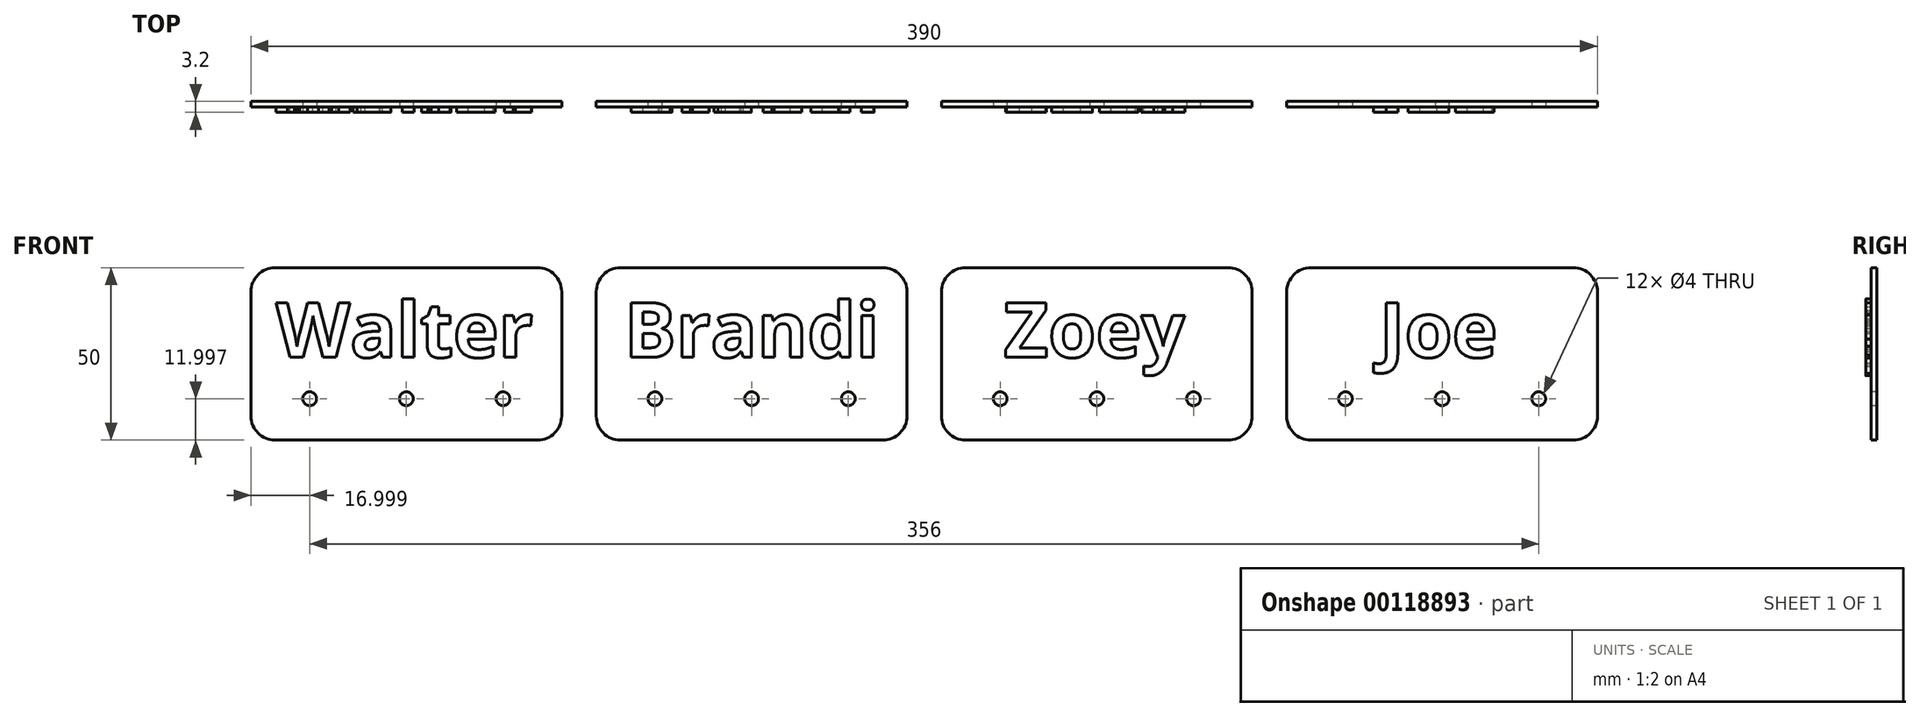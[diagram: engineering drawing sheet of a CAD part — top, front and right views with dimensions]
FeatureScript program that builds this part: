
annotation { "Feature Type Name" : "Feature", "Feature Type Description" : "" }
export const myFeature = defineFeature(function(context is Context, id is Id, definition is map)
    precondition{}
    {
        {
            var Q0;
            Q0=qCreatedBy(makeId("Front.planeOp"),FACE);
            var sketch = newSketch(context, id + "F0", { "sketchPlane" : qUnion([Q0])});
            skLineSegment(sketch, "E0.bottom", {"start": v(-28.01, 48.34) * mm, "end": v(47.99, 48.34) * mm});
            skLineSegment(sketch, "E0.top", {"start": v(-28.01, -1.66) * mm, "end": v(47.99, -1.66) * mm});
            skLineSegment(sketch, "E0.left", {"start": v(-35.01, 41.34) * mm, "end": v(-35.01, 5.34) * mm});
            skLineSegment(sketch, "E0.right", {"start": v(54.99, 41.34) * mm, "end": v(54.99, 5.34) * mm});
            skLineSegment(sketch, "E1", {"start": v(-35.01, 10.34) * mm, "end": v(54.99, 10.34) * mm, "construction": true});
            skLineSegment(sketch, "E2", {"start": v(-35.01, 22.34) * mm, "end": v(54.99, 22.34) * mm, "construction": true});
            skLineSegment(sketch, "E3", {"start": v(-35.01, 38.34) * mm, "end": v(54.99, 38.34) * mm, "construction": true});
            skPoint(sketch, "E4.visualSharp", {"position": v(-35.01, 48.34) * mm});
            skArc(sketch, "E4.filletArc", {"start": v(-28.01, 48.34) * mm, "mid": v(-32.96, 46.29) * mm, "end": v(-35.01, 41.34) * mm});
            skPoint(sketch, "E5.visualSharp", {"position": v(54.99, 48.34) * mm});
            skArc(sketch, "E5.filletArc", {"start": v(54.99, 41.34) * mm, "mid": v(52.94, 46.29) * mm, "end": v(47.99, 48.34) * mm});
            skPoint(sketch, "E6.visualSharp", {"position": v(54.99, -1.66) * mm});
            skArc(sketch, "E6.filletArc", {"start": v(47.99, -1.66) * mm, "mid": v(52.94, 0.39) * mm, "end": v(54.99, 5.34) * mm});
            skPoint(sketch, "E7.visualSharp", {"position": v(-35.01, -1.66) * mm});
            skArc(sketch, "E7.filletArc", {"start": v(-35.01, 5.34) * mm, "mid": v(-32.96, 0.39) * mm, "end": v(-28.01, -1.66) * mm});
            skLineSegment(sketch, "E8", {"start": v(9.99, 48.34) * mm, "end": v(9.99, -1.66) * mm, "construction": true});
            skCircle(sketch, "E9", {"center": v(-18.01, 10.34) * mm, "radius": 2 * mm});
            skCircle(sketch, "E10", {"center": v(9.99, 10.34) * mm, "radius": 2 * mm});
            skCircle(sketch, "E11.MirrorC", {"center": v(37.99, 10.34) * mm, "radius": 2 * mm});
            skLineSegment(sketch, "E12.1.0.0", {"start": v(64.99, 41.34) * mm, "end": v(64.99, 5.34) * mm});
            skArc(sketch, "E12.1.0.1", {"start": v(71.99, 48.34) * mm, "mid": v(67.04, 46.29) * mm, "end": v(64.99, 41.34) * mm});
            skPoint(sketch, "E12.1.0.2", {"position": v(154.99, -1.66) * mm});
            skLineSegment(sketch, "E12.1.0.3", {"start": v(64.99, 38.34) * mm, "end": v(154.99, 38.34) * mm, "construction": true});
            skArc(sketch, "E12.1.0.4", {"start": v(147.99, -1.66) * mm, "mid": v(152.94, 0.39) * mm, "end": v(154.99, 5.34) * mm});
            skLineSegment(sketch, "E12.1.0.5", {"start": v(64.99, 22.34) * mm, "end": v(154.99, 22.34) * mm, "construction": true});
            skLineSegment(sketch, "E12.1.0.6", {"start": v(64.99, 10.34) * mm, "end": v(154.99, 10.34) * mm, "construction": true});
            skLineSegment(sketch, "E12.1.0.7", {"start": v(154.99, 41.34) * mm, "end": v(154.99, 5.34) * mm});
            skArc(sketch, "E12.1.0.8", {"start": v(64.99, 5.34) * mm, "mid": v(67.04, 0.39) * mm, "end": v(71.99, -1.66) * mm});
            skLineSegment(sketch, "E12.1.0.9", {"start": v(109.99, 48.34) * mm, "end": v(109.99, -1.66) * mm, "construction": true});
            skLineSegment(sketch, "E12.1.0.10", {"start": v(71.99, -1.66) * mm, "end": v(147.99, -1.66) * mm});
            skPoint(sketch, "E12.1.0.11", {"position": v(154.99, 48.34) * mm});
            skCircle(sketch, "E12.1.0.12", {"center": v(81.99, 10.34) * mm, "radius": 2 * mm});
            skCircle(sketch, "E12.1.0.13", {"center": v(109.99, 10.34) * mm, "radius": 2 * mm});
            skArc(sketch, "E12.1.0.14", {"start": v(154.99, 41.34) * mm, "mid": v(152.94, 46.29) * mm, "end": v(147.99, 48.34) * mm});
            skCircle(sketch, "E12.1.0.15", {"center": v(137.99, 10.34) * mm, "radius": 2 * mm});
            skPoint(sketch, "E12.1.0.16", {"position": v(64.99, 48.34) * mm});
            skLineSegment(sketch, "E12.1.0.17", {"start": v(71.99, 48.34) * mm, "end": v(147.99, 48.34) * mm});
            skPoint(sketch, "E12.1.0.18", {"position": v(64.99, -1.66) * mm});
            skLineSegment(sketch, "E12.2.0.0", {"start": v(164.99, 41.34) * mm, "end": v(164.99, 5.34) * mm});
            skArc(sketch, "E12.2.0.1", {"start": v(171.99, 48.34) * mm, "mid": v(167.04, 46.29) * mm, "end": v(164.99, 41.34) * mm});
            skPoint(sketch, "E12.2.0.2", {"position": v(254.99, -1.66) * mm});
            skLineSegment(sketch, "E12.2.0.3", {"start": v(164.99, 38.34) * mm, "end": v(254.99, 38.34) * mm, "construction": true});
            skArc(sketch, "E12.2.0.4", {"start": v(247.99, -1.66) * mm, "mid": v(252.94, 0.39) * mm, "end": v(254.99, 5.34) * mm});
            skLineSegment(sketch, "E12.2.0.5", {"start": v(164.99, 22.34) * mm, "end": v(254.99, 22.34) * mm, "construction": true});
            skLineSegment(sketch, "E12.2.0.6", {"start": v(164.99, 10.34) * mm, "end": v(254.99, 10.34) * mm, "construction": true});
            skLineSegment(sketch, "E12.2.0.7", {"start": v(254.99, 41.34) * mm, "end": v(254.99, 5.34) * mm});
            skArc(sketch, "E12.2.0.8", {"start": v(164.99, 5.34) * mm, "mid": v(167.04, 0.39) * mm, "end": v(171.99, -1.66) * mm});
            skLineSegment(sketch, "E12.2.0.9", {"start": v(209.99, 48.34) * mm, "end": v(209.99, -1.66) * mm, "construction": true});
            skLineSegment(sketch, "E12.2.0.10", {"start": v(171.99, -1.66) * mm, "end": v(247.99, -1.66) * mm});
            skPoint(sketch, "E12.2.0.11", {"position": v(254.99, 48.34) * mm});
            skCircle(sketch, "E12.2.0.12", {"center": v(181.99, 10.34) * mm, "radius": 2 * mm});
            skCircle(sketch, "E12.2.0.13", {"center": v(209.99, 10.34) * mm, "radius": 2 * mm});
            skArc(sketch, "E12.2.0.14", {"start": v(254.99, 41.34) * mm, "mid": v(252.94, 46.29) * mm, "end": v(247.99, 48.34) * mm});
            skCircle(sketch, "E12.2.0.15", {"center": v(237.99, 10.34) * mm, "radius": 2 * mm});
            skPoint(sketch, "E12.2.0.16", {"position": v(164.99, 48.34) * mm});
            skLineSegment(sketch, "E12.2.0.17", {"start": v(171.99, 48.34) * mm, "end": v(247.99, 48.34) * mm});
            skPoint(sketch, "E12.2.0.18", {"position": v(164.99, -1.66) * mm});
            skLineSegment(sketch, "E12.3.0.0", {"start": v(264.99, 41.34) * mm, "end": v(264.99, 5.34) * mm});
            skArc(sketch, "E12.3.0.1", {"start": v(271.99, 48.34) * mm, "mid": v(267.04, 46.29) * mm, "end": v(264.99, 41.34) * mm});
            skPoint(sketch, "E12.3.0.2", {"position": v(354.99, -1.66) * mm});
            skLineSegment(sketch, "E12.3.0.3", {"start": v(264.99, 38.34) * mm, "end": v(354.99, 38.34) * mm, "construction": true});
            skArc(sketch, "E12.3.0.4", {"start": v(347.99, -1.66) * mm, "mid": v(352.94, 0.39) * mm, "end": v(354.99, 5.34) * mm});
            skLineSegment(sketch, "E12.3.0.5", {"start": v(264.99, 22.34) * mm, "end": v(354.99, 22.34) * mm, "construction": true});
            skLineSegment(sketch, "E12.3.0.6", {"start": v(264.99, 10.34) * mm, "end": v(354.99, 10.34) * mm, "construction": true});
            skLineSegment(sketch, "E12.3.0.7", {"start": v(354.99, 41.34) * mm, "end": v(354.99, 5.34) * mm});
            skArc(sketch, "E12.3.0.8", {"start": v(264.99, 5.34) * mm, "mid": v(267.04, 0.39) * mm, "end": v(271.99, -1.66) * mm});
            skLineSegment(sketch, "E12.3.0.9", {"start": v(309.99, 48.34) * mm, "end": v(309.99, -1.66) * mm, "construction": true});
            skLineSegment(sketch, "E12.3.0.10", {"start": v(271.99, -1.66) * mm, "end": v(347.99, -1.66) * mm});
            skPoint(sketch, "E12.3.0.11", {"position": v(354.99, 48.34) * mm});
            skCircle(sketch, "E12.3.0.12", {"center": v(281.99, 10.34) * mm, "radius": 2 * mm});
            skCircle(sketch, "E12.3.0.13", {"center": v(309.99, 10.34) * mm, "radius": 2 * mm});
            skArc(sketch, "E12.3.0.14", {"start": v(354.99, 41.34) * mm, "mid": v(352.94, 46.29) * mm, "end": v(347.99, 48.34) * mm});
            skCircle(sketch, "E12.3.0.15", {"center": v(337.99, 10.34) * mm, "radius": 2 * mm});
            skPoint(sketch, "E12.3.0.16", {"position": v(264.99, 48.34) * mm});
            skLineSegment(sketch, "E12.3.0.17", {"start": v(271.99, 48.34) * mm, "end": v(347.99, 48.34) * mm});
            skPoint(sketch, "E12.3.0.18", {"position": v(264.99, -1.66) * mm});
            skLineSegment(sketch, "E12.direction1", {"start": v(-35.01, -1.66) * mm, "end": v(64.99, -1.66) * mm, "construction": true});
            skSolve(sketch);
        }
        {
            var Q0;
            Q0=makeQuery(id+"F0.imprint","IMPRINT",FACE,{"disambiguationData":[TD([[makeQuery(id+"F0.imprint","IMPRINT",EDGE,{"derivedFrom":sQuery(id+"F0.wireOp",EDGE,"E12.1.0.0")}),1.0]])]});
            var Q1;
            Q1=makeQuery(id+"F0.imprint","IMPRINT",FACE,{"disambiguationData":[TD([[makeQuery(id+"F0.imprint","IMPRINT",EDGE,{"derivedFrom":sQuery(id+"F0.wireOp",EDGE,"E12.2.0.0")}),1.0]])]});
            var Q2;
            Q2=makeQuery(id+"F0.imprint","IMPRINT",FACE,{"disambiguationData":[TD([[makeQuery(id+"F0.imprint","IMPRINT",EDGE,{"derivedFrom":sQuery(id+"F0.wireOp",EDGE,"E0.bottom")}),-1.0]])]});
            var Q3;
            Q3=makeQuery(id+"F0.imprint","IMPRINT",FACE,{"disambiguationData":[TD([[makeQuery(id+"F0.imprint","IMPRINT",EDGE,{"derivedFrom":sQuery(id+"F0.wireOp",EDGE,"E12.3.0.0")}),1.0]])]});
            extrude(context, id + "F1", {"entities" : qUnion([Q0, Q1, Q2, Q3]), "oppositeDirection" : true, "depth" : 1.6 * mm});
        }
        {
            var Q0;
            Q0=makeQuery(id+"F1.opExtrude","CAP_FACE",FACE,{"disambiguationData":[OSD([sQuery(id+"F0.wireOp",EDGE,"E0.bottom"),sQuery(id+"F0.wireOp",EDGE,"E0.top"),sQuery(id+"F0.wireOp",EDGE,"E0.left"),sQuery(id+"F0.wireOp",EDGE,"E0.right"),sQuery(id+"F0.wireOp",EDGE,"E4.filletArc"),sQuery(id+"F0.wireOp",EDGE,"E5.filletArc"),sQuery(id+"F0.wireOp",EDGE,"E6.filletArc"),sQuery(id+"F0.wireOp",EDGE,"E7.filletArc"),sQuery(id+"F0.wireOp",EDGE,"E9"),sQuery(id+"F0.wireOp",EDGE,"E10"),sQuery(id+"F0.wireOp",EDGE,"E11.MirrorC")])],"isStart":true});
            var sketch = newSketch(context, id + "F2", { "sketchPlane" : qUnion([Q0])});
            skLineSegment(sketch, "E13.0", {"start": v(-35.01, 38.34) * mm, "end": v(54.99, 38.34) * mm, "construction": true});
            skLineSegment(sketch, "E14.0", {"start": v(-35.01, 22.34) * mm, "end": v(54.99, 22.34) * mm, "construction": true});
            skLineSegment(sketch, "E15.0", {"start": v(9.99, 48.34) * mm, "end": v(9.99, -1.66) * mm, "construction": true});
            skText(sketch, "E16", { "text": "Walter", "fontName": "OpenSans-Bold.ttf"});
            const initialGuessF2  = {"E16": [-0.02778, 0.02234, 1, 0, 0.016]};
            skSetInitialGuess(sketch, initialGuessF2);
            skSolve(sketch);
        }
        {
            var Q0;
            Q0 = qSketchRegion(id + "F2", true);
            extrude(context, id + "F3", {"entities" : qUnion([Q0]), "operationType" : NewBodyOperationType.ADD, "depth" : 1.6 * mm});
        }
        {
            var Q0;
            Q0=makeQuery(id+"F0.imprint","IMPRINT",FACE,{"disambiguationData":[TD([[makeQuery(id+"F0.imprint","IMPRINT",EDGE,{"derivedFrom":sQuery(id+"F0.wireOp",EDGE,"E12.1.0.0")}),1.0]])]});
            var sketch = newSketch(context, id + "F4", { "sketchPlane" : qUnion([Q0])});
            skLineSegment(sketch, "E17.0", {"start": v(64.99, 38.34) * mm, "end": v(154.99, 38.34) * mm, "construction": true});
            skLineSegment(sketch, "E18.0", {"start": v(64.99, 22.34) * mm, "end": v(154.99, 22.34) * mm, "construction": true});
            skLineSegment(sketch, "E19.0", {"start": v(109.99, 48.34) * mm, "end": v(109.99, -1.66) * mm, "construction": true});
            skText(sketch, "E20", { "text": "Brandi", "fontName": "OpenSans-Bold.ttf"});
            const initialGuessF4  = {"E20": [0.07311, 0.02234, 1, 0, 0.016]};
            skSetInitialGuess(sketch, initialGuessF4);
            skSolve(sketch);
        }
        {
            var Q0;
            Q0 = qSketchRegion(id + "F4", true);
            extrude(context, id + "F5", {"entities" : qUnion([Q0]), "operationType" : NewBodyOperationType.ADD, "depth" : 1.6 * mm});
        }
        {
            var Q0;
            Q0=makeQuery(id+"F0.imprint","IMPRINT",FACE,{"disambiguationData":[TD([[makeQuery(id+"F0.imprint","IMPRINT",EDGE,{"derivedFrom":sQuery(id+"F0.wireOp",EDGE,"E12.2.0.0")}),1.0]])]});
            var sketch = newSketch(context, id + "F6", { "sketchPlane" : qUnion([Q0])});
            skLineSegment(sketch, "E21.0", {"start": v(164.99, 38.34) * mm, "end": v(254.99, 38.34) * mm, "construction": true});
            skLineSegment(sketch, "E22.0", {"start": v(209.99, 48.34) * mm, "end": v(209.99, -1.66) * mm, "construction": true});
            skLineSegment(sketch, "E23.0", {"start": v(164.99, 22.34) * mm, "end": v(254.99, 22.34) * mm, "construction": true});
            skText(sketch, "E24", { "text": "Zoey", "fontName": "OpenSans-Bold.ttf"});
            const initialGuessF6  = {"E24": [0.18307, 0.02234, 1, 0, 0.016]};
            skSetInitialGuess(sketch, initialGuessF6);
            skSolve(sketch);
        }
        {
            var Q0;
            Q0 = qSketchRegion(id + "F6", true);
            extrude(context, id + "F7", {"entities" : qUnion([Q0]), "operationType" : NewBodyOperationType.ADD, "depth" : 1.6 * mm});
        }
        {
            var Q0;
            Q0=makeQuery(id+"F0.imprint","IMPRINT",FACE,{"disambiguationData":[TD([[makeQuery(id+"F0.imprint","IMPRINT",EDGE,{"derivedFrom":sQuery(id+"F0.wireOp",EDGE,"E12.3.0.0")}),1.0]])]});
            var sketch = newSketch(context, id + "F8", { "sketchPlane" : qUnion([Q0])});
            skLineSegment(sketch, "E25.0", {"start": v(309.99, 48.34) * mm, "end": v(309.99, -1.66) * mm, "construction": true});
            skLineSegment(sketch, "E26.0", {"start": v(264.99, 22.34) * mm, "end": v(354.99, 22.34) * mm, "construction": true});
            skLineSegment(sketch, "E27.0", {"start": v(264.99, 38.34) * mm, "end": v(354.99, 38.34) * mm, "construction": true});
            skText(sketch, "E28", { "text": "Joe", "fontName": "OpenSans-Bold.ttf"});
            const initialGuessF8  = {"E28": [0.2918, 0.02234, 1, 0, 0.016]};
            skSetInitialGuess(sketch, initialGuessF8);
            skSolve(sketch);
        }
        {
            var Q0;
            Q0 = qSketchRegion(id + "F8", true);
            extrude(context, id + "F9", {"entities" : qUnion([Q0]), "operationType" : NewBodyOperationType.ADD, "depth" : 1.6 * mm});
        }
    });
